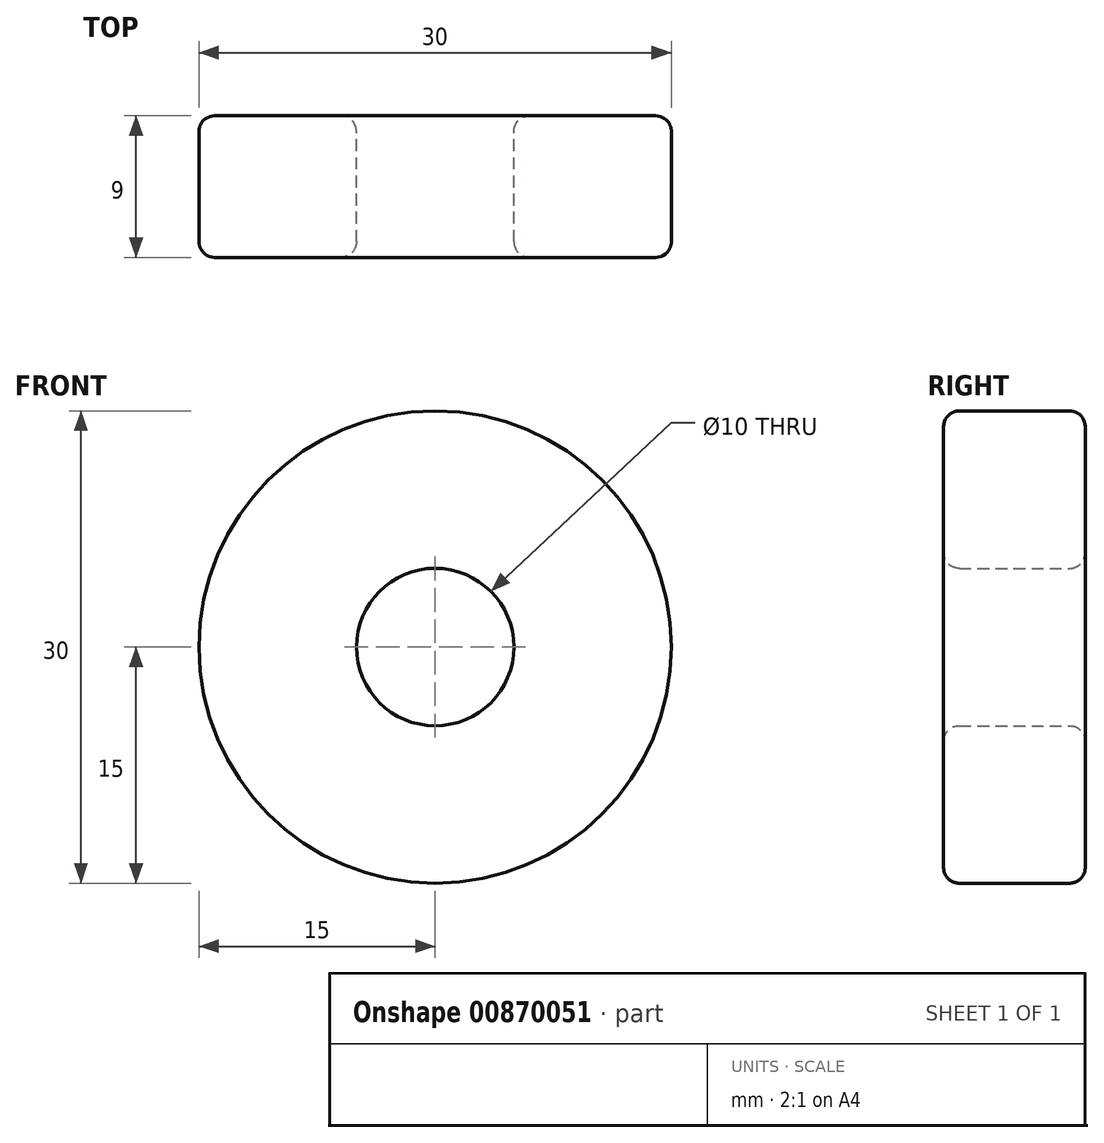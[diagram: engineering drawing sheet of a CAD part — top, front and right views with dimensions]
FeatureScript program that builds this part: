
annotation { "Feature Type Name" : "Feature", "Feature Type Description" : "" }
export const myFeature = defineFeature(function(context is Context, id is Id, definition is map)
    precondition{}
    {
        {
            var Q0;
            Q0=qCreatedBy(makeId("Front.planeOp"),FACE);
            var sketch = newSketch(context, id + "F0", { "sketchPlane" : qUnion([Q0])});
            skCircle(sketch, "E0", {"center": v(0, 0) * mm, "radius": 15 * mm});
            skCircle(sketch, "E1", {"center": v(0, 0) * mm, "radius": 5 * mm});
            skSolve(sketch);
        }
        {
            var Q0;
            Q0 = qSketchRegion(id + "F0", true);
            extrude(context, id + "F1", {"entities" : qUnion([Q0]), "depth" : 9 * mm, "offsetDistance" : 25.4 * mm});
        }
        {
            var Q0;
            Q0=makeQuery(id+"F1.opExtrude","SWEPT_FACE",FACE,{"disambiguationData":[OSD([sQuery(id+"F0.wireOp",EDGE,"E0")])]});
            var Q1;
            Q1=makeQuery(id+"F1.opExtrude","SWEPT_FACE",FACE,{"disambiguationData":[OSD([sQuery(id+"F0.wireOp",EDGE,"E1")])]});
            fillet(context, id + "F2", {"entities" : qUnion([Q0, Q1]), "radius" : 1 * mm, "tangentPropagation" : true, "allowEdgeOverflow" : false});
        }
    });
